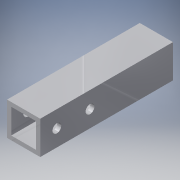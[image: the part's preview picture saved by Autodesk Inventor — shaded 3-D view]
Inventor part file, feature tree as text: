
AUTODESK INVENTOR PART (.ipt)
format: ipt  version: 2016 (Build 200138000, 138)  size: 122,880 bytes
history: native  units: in
note: dims shown in document units (in); Inventor stores cm internally (conversion verified against a paired STEP export)
features: extrude x2, sketch x2
ambient origin geometry x8: Origin, YZ Plane, XZ Plane, XY Plane, X Axis, Y Axis, Z Axis, Center Point
bodies: Solid1 (feature_tree)
feature tree (4):
  extrude  "Extrusion1"  Depth=2.0in
  extrude  "Extrusion3"  Depth=0.125in
  sketch  "Sketch1"  dims[d0=1.0in d1=2.0in]
  sketch  "Sketch2"  dims[d2=0.125in d3=0.125in d4=0.125in d5=0.125in d6=4.0in d7=0.0in d8=0.2656in d12=2.5in d13=3.5in d14=0.5in d17=1.5in d18=1.0in d19=0.0in d27=0.6in d28=0.5in d29=1.5in d30=0.5in]
